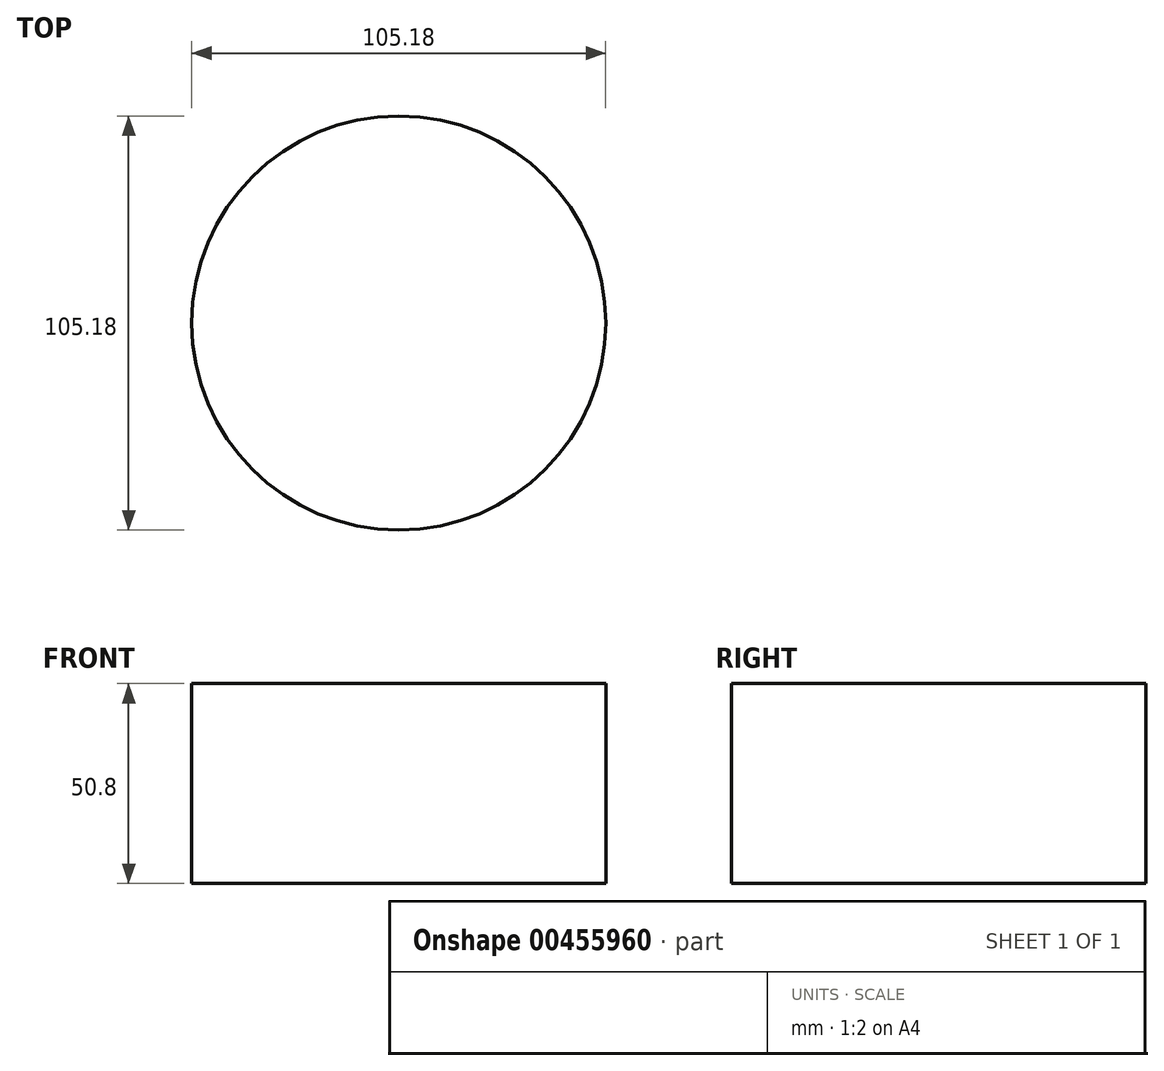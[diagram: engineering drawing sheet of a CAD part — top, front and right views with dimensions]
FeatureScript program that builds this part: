
annotation { "Feature Type Name" : "Feature", "Feature Type Description" : "" }
export const myFeature = defineFeature(function(context is Context, id is Id, definition is map)
    precondition{}
    {
        {
            var Q0;
            Q0=qCreatedBy(makeId("Top.planeOp"),FACE);
            var sketch = newSketch(context, id + "F0", { "sketchPlane" : qUnion([Q0])});
            skCircle(sketch, "E0", {"center": v(0, 0) * mm, "radius": 52.6 * mm});
            skSolve(sketch);
        }
        {
            var Q0;
            Q0 = qSketchRegion(id + "F0", true);
            extrude(context, id + "F1", {"entities" : qUnion([Q0]), "depth" : 50.8 * mm});
        }
    });
